# Revit family: Faucet_Bathroom-DXV-Ashbee-D351018XX_Series
name_source: partatom
category: Plumbing Fixtures
revit_build: Autodesk Revit 2014 (Build: 20130308_1515(x64)
units: mm (PartAtom-declared; Revit-internal decimal feet)

## types (12) — shared parameters
Assembly Code = D2020300
CW Connection = Yes
CWFU = 1.5
Cold Water Connection Diameter = 1/2"
Default Elevation = 0"
Description = Ashbee Widespread Lavatory Faucet
HW Connection = Yes
HWFU = 1.5
Height = 5 15/16"
Hot Water Connection Diameter = 1"
Installation Type = Deck Mounted
Length = 5 1/8"
Manufacturer = DXV
Price = Prices may vary. Please consult Manufacturer Representative for most up-to-date price list.
Product Documentation Link = https://dxv01.blob.core.windows.net
Product Page URL = https://www.dxv.com
Revised Date = 20/09/2017
URL = http://www.dxv.com
Vent Connection = No
WFU = 2
Warranty Documentation Link = https://www.dxv.com
Waste Connection = No

## per-type parameters (varying)
| type | ADA Compliant | Cross Handle Option | Finish | Flow Rate | Lever Handle Option | Material | Model | Width |
| D35101840.144 | No | Yes | Metal-DXV-144-Brushed Nickel | 1.5 GPM (5.7L/min) | No | Metal-DXV-144-Brushed Nickel | D35101840.144 | 8" |
| D35101840.100 | No | Yes | Metal-DXV-100-Polished Chrome | 1.5 GPM (5.7L/min) | No | Metal-DXV-100-Polished Chrome | D35101840.100 | 8" |
| D35101840.150 | No | Yes | Metal-DXV-150-Platinum Nickel | 1.5 GPM (5.7L/min) | No | Metal-DXV-150-Platinum Nickel | D35101840.150 | 8" |
| D35101800.100 | Yes | No | Metal-DXV-100-Polished Chrome | 1.5 GPM (5.7L/min) | Yes | Metal-DXV-100-Polished Chrome | D35101800.100 | 10" |
| D35101800.144 | Yes | No | Metal-DXV-144-Brushed Nickel | 1.5 GPM (5.7L/min) | Yes | Metal-DXV-150-Platinum Nickel | D35101800.144 | 8" |
| D35101800.150 | Yes | No | Metal-DXV-150-Platinum Nickel | 1.5 GPM (5.7L/min) | Yes | Metal-DXV-150-Platinum Nickel | D35101840.150 | 8" |
| D3510180C.100 | Yes | No | Metal-DXV-100-Polished Chrome | 1.2 gpm (4.5 L/min) | Yes | Metal-DXV-100-Polished Chrome | D3510180C.100 | 8" |
| D3510180C.144 | Yes | No | Metal-DXV-144-Brushed Nickel | 1.2 gpm (4.5 L/min) | Yes | Metal-DXV-150-Platinum Nickel | D3510180C.144 | 8" |
| D3510180C.150 | Yes | No | Metal-DXV-150-Platinum Nickel | 1.2 gpm (4.5 L/min) | Yes | Metal-DXV-150-Platinum Nickel | D35101840.150 | 8" |
| D3510184C.100 | No | Yes | Metal-DXV-100-Polished Chrome | 1.2 gpm (4.5 L/min) | No | Metal-DXV-100-Polished Chrome | D3510184C.100 | 8" |
| D3510184C.144 | No | Yes | Metal-DXV-144-Brushed Nickel | 1.2 gpm (4.5 L/min) | No | Metal-DXV-144-Brushed Nickel | D3510184C.144 | 8" |
| D3510184C.150 | No | Yes | Metal-DXV-150-Platinum Nickel | 1.2 gpm (4.5 L/min) | No | Metal-DXV-150-Platinum Nickel | D3510184C.150 | 8" |

## geometry (parser evidence)
native form markers: Sweep x2
no freeform markers — native parametric forms only
